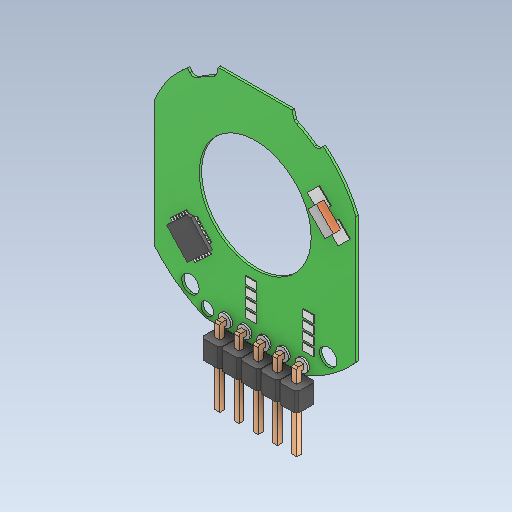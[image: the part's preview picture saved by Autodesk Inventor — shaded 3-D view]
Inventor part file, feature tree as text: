
AUTODESK INVENTOR PART (.ipt)
format: ipt  version: 2020 (Build 240168000, 168)  size: 452,608 bytes
history: native  units: in
note: dims shown in document units (in); Inventor stores cm internally (conversion verified against a paired STEP export)
features: other x4, extrude x3
ambient origin geometry x8: Origin, YZ Plane, XZ Plane, XY Plane, X Axis, Y Axis, Z Axis, Center Point
bodies: Solid1 (feature_tree), Solid2 (feature_tree), Solid3 (feature_tree), Solid4 (feature_tree), Solid5 (feature_tree), Solid6 (feature_tree), Solid7 (feature_tree)
feature tree (7):
  extrude  "Extrude3"  [1 undecoded]
  extrude  "Extrude4"  [1 undecoded]
  extrude  "Extrude15"  [1 undecoded]
  other  "LPattern9[1]"
  other  "LPattern9[2]"
  other  "LPattern9[3]"
  other  "LPattern9[4]"
note: 3 required parameter values undecoded (feature->parameter linkage not recoverable at this tier; creation-order binding heuristic only, values carry confidence <= 0.55)
